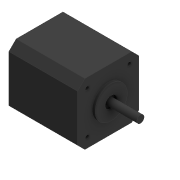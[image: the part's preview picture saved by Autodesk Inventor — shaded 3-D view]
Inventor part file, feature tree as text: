
AUTODESK INVENTOR PART (.ipt)
format: ipt  version: 2020 (Build 240168000, 168)  size: 147,968 bytes
history: native  units: in
note: dims shown in document units (in); Inventor stores cm internally (conversion verified against a paired STEP export)
features: extrude x4, sketch x4, chamfer x1
ambient origin geometry x8: Origin, YZ Plane, XZ Plane, XY Plane, X Axis, Y Axis, Z Axis, Center Point
bodies: Solid1 (feature_tree)
feature tree (9):
  extrude  "Extrusion1"  Depth=1.6535in
  extrude  "Extrusion2"  Depth=0.8661in
  extrude  "Extrusion3"  Depth=0.0787in TaperAngle=0.0deg
  chamfer  "Chamfer1"  Distance=0.8661in
  extrude  "Extrusion4"  Depth=0.1969in TaperAngle=45.0deg
  sketch  "Sketch1"  dims[d0=1.6535in d1=1.6535in]
  sketch  "Sketch2"  dims[d2=1.8504in d3=0.0in d4=0.8661in]
  sketch  "Sketch3"  dims[d5=0.315in d6=0.0787in d7=0.0in]
  sketch  "Sketch4"  dims[d8=0.1969in d9=0.8661in d10=0.0in d11=0.1969in d12=0.125in d13=45.0deg d14=1.1319in d15=1.1319in d16=0.2608in d17=0.2608in d18=0.0984in d19=0.0984in d20=0.0984in d21=0.0984in d22=0.1969in d23=0.0in]
